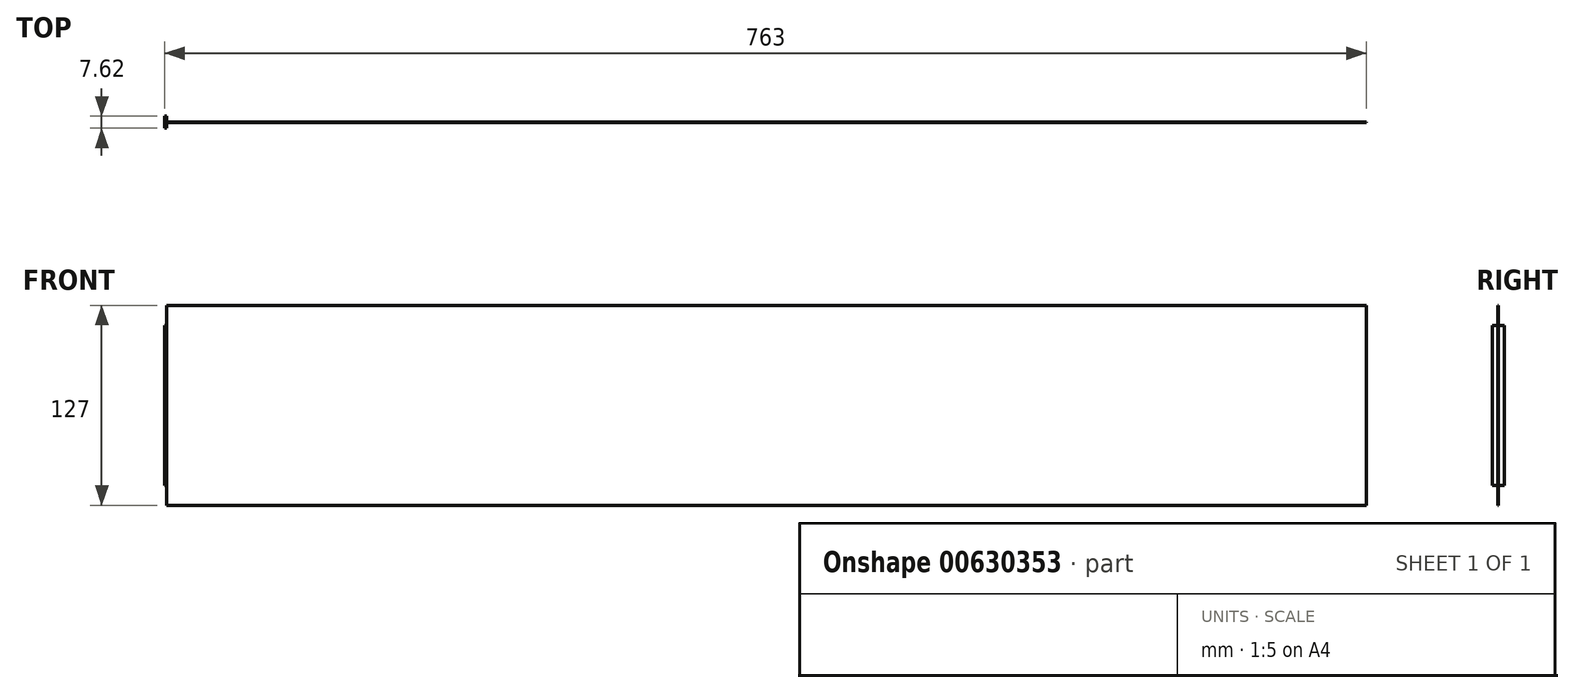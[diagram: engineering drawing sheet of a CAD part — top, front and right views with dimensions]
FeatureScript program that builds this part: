
annotation { "Feature Type Name" : "Feature", "Feature Type Description" : "" }
export const myFeature = defineFeature(function(context is Context, id is Id, definition is map)
    precondition{}
    {
        {
            assignVariable(context, id + "F0", {"name" : "traverse_epaisseur", "anyValue" : 0.5});
        }
        {
            assignVariable(context, id + "F1", {"name" : "tenon_profondeur", "anyValue" : 1});
        }
        {
            var Q0;
            Q0=qCreatedBy(makeId("Front.planeOp"),FACE);
            var sketch = newSketch(context, id + "F2", { "sketchPlane" : qUnion([Q0])});
            skLineSegment(sketch, "E0.bottom", {"start": v(-381, 63.5) * mm, "end": v(381, 63.5) * mm});
            skLineSegment(sketch, "E0.top", {"start": v(-381, -63.5) * mm, "end": v(381, -63.5) * mm});
            skLineSegment(sketch, "E0.left", {"start": v(-381, 63.5) * mm, "end": v(-381, -63.5) * mm});
            skLineSegment(sketch, "E0.right", {"start": v(381, 63.5) * mm, "end": v(381, -63.5) * mm});
            skPoint(sketch, "E0.middle", {"position": v(0, 0) * mm});
            skSolve(sketch);
        }
        {
            var Q0;
            Q0 = qSketchRegion(id + "F2", true);
            extrude(context, id + "F3", {"entities" : qUnion([Q0]), "endBound" : BoundingType.SYMMETRIC, "depth" : (getVariable(context, 'traverse_epaisseur')) * mm, "offsetDistance" : 25.4 * mm});
        }
        {
            var Q0;
            Q0=makeQuery(id+"F3.opExtrude","SWEPT_FACE",FACE,{"disambiguationData":[OSD([sQuery(id+"F2.wireOp",EDGE,"E0.left")])]});
            var sketch = newSketch(context, id + "F4", { "sketchPlane" : qUnion([Q0])});
            skLineSegment(sketch, "E1.bottom", {"start": v(-3.81, 50.8) * mm, "end": v(3.81, 50.8) * mm});
            skLineSegment(sketch, "E1.top", {"start": v(-3.81, -50.8) * mm, "end": v(3.81, -50.8) * mm});
            skLineSegment(sketch, "E1.left", {"start": v(-3.81, 50.8) * mm, "end": v(-3.81, -50.8) * mm});
            skLineSegment(sketch, "E1.right", {"start": v(3.81, 50.8) * mm, "end": v(3.81, -50.8) * mm});
            skPoint(sketch, "E1.middle", {"position": v(0, 0) * mm});
            skSolve(sketch);
        }
        {
            var Q0;
            Q0=makeQuery(id+"F4.imprint","IMPRINT",FACE,{"disambiguationData":[TD([[makeQuery(id+"F4.imprint","IMPRINT",EDGE,{"derivedFrom":sQuery(id+"F4.wireOp",EDGE,"E1.bottom")}),-1.0]])]});
            extrude(context, id + "F5", {"entities" : qUnion([Q0]), "operationType" : NewBodyOperationType.ADD, "depth" : (getVariable(context, 'tenon_profondeur')) * mm, "offsetDistance" : 25.4 * mm});
        }
    });
